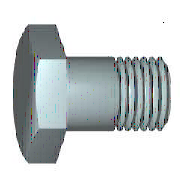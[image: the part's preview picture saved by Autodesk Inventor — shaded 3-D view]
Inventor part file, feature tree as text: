
AUTODESK INVENTOR PART (.ipt)
format: ipt  version: 2019 (Build 230136000, 136)  size: 188,928 bytes
history: native  units: mm (DEFAULTED — no unit token found)
features: sketch x3, extrude x1, chamfer x1, plane x1
ambient origin geometry x7: Origin, YZ Plane, XZ Plane, X Axis, Y Axis, Z Axis, Center Point
bodies: Solid1 (feature_tree), Body (feature_tree)
feature tree (6):
  extrude  "Head"  Depth=16.0mm
  chamfer  "Chamfer1"  Distance=3.0mm
  plane  "Work Plane1"
  sketch  "Sketch1"  dims[d0=40.0mm d1=16.0mm]
  sketch  "Sketch2"  dims[d2=5.0mm]
  sketch  "Sketch4"  dims[d12=90.0deg d3=3.0mm d4=0.0mm d5=30.0deg d21=90.0deg d6=0.49076mm d7=0.49086mm d8=0.0mm d9=0.5001mm d10=6.9mm d11=8.0mm d13=0.49086mm d14=5.0mm d15=16.0mm d16=0.0mm d19=8.0mm d55=45.0deg d57=0.0mm d58=0.0mm]
